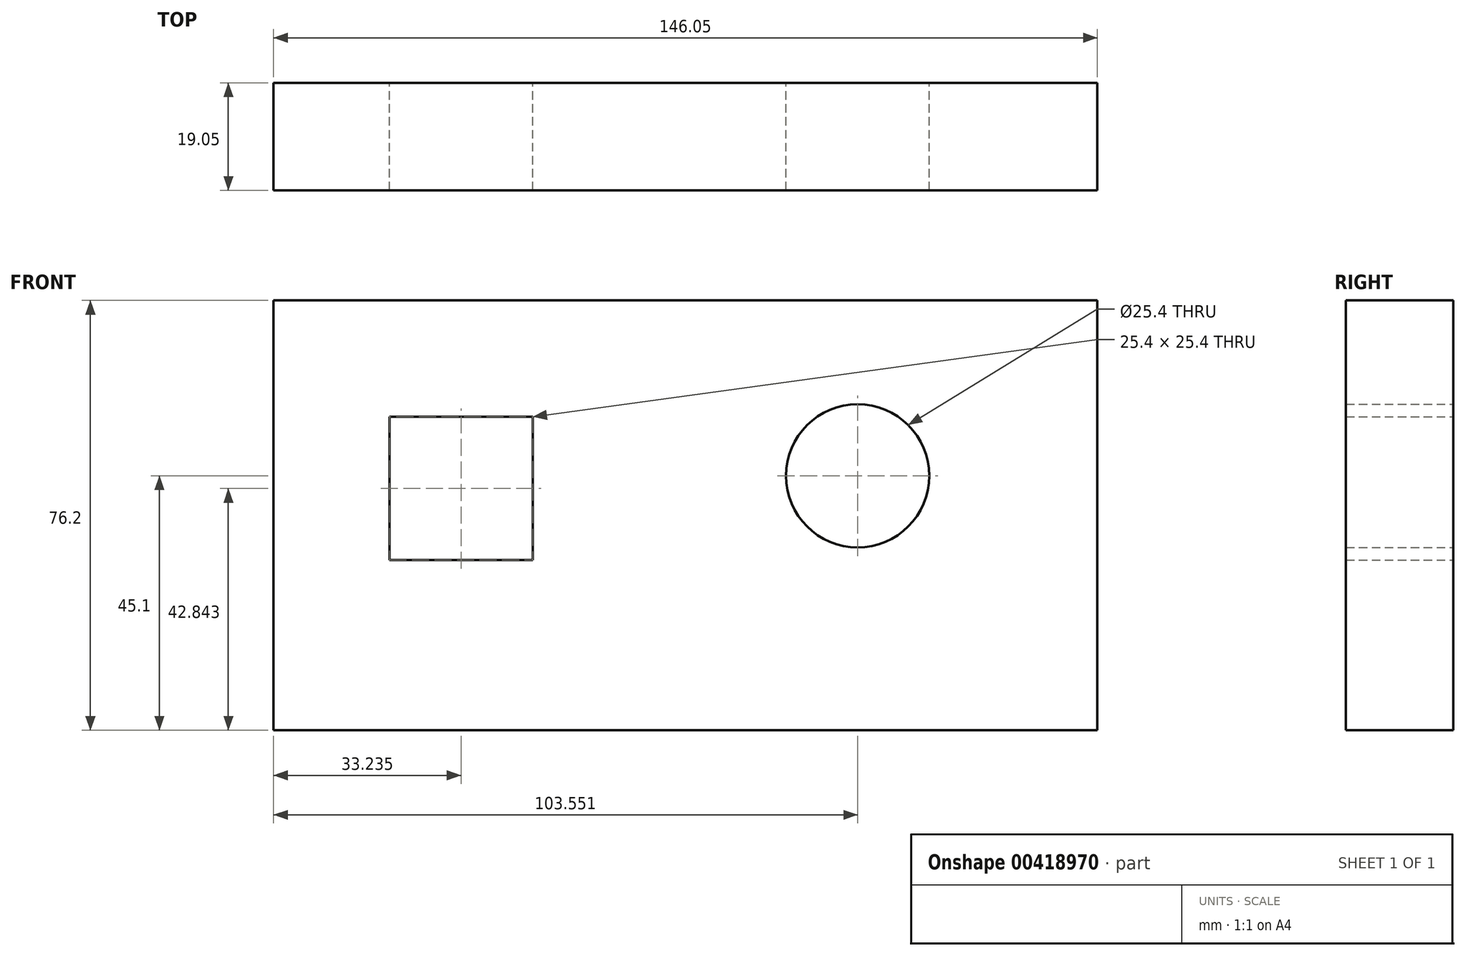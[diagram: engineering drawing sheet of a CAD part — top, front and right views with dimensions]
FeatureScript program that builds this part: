
annotation { "Feature Type Name" : "Feature", "Feature Type Description" : "" }
export const myFeature = defineFeature(function(context is Context, id is Id, definition is map)
    precondition{}
    {
        {
            var Q0;
            Q0=qCreatedBy(makeId("Front.planeOp"),FACE);
            var sketch = newSketch(context, id + "F0", { "sketchPlane" : qUnion([Q0])});
            skLineSegment(sketch, "E0.bottom", {"start": v(-73.5, 31.1) * mm, "end": v(72.55, 31.1) * mm});
            skLineSegment(sketch, "E0.top", {"start": v(-73.5, -45.1) * mm, "end": v(72.55, -45.1) * mm});
            skLineSegment(sketch, "E0.left", {"start": v(-73.5, 31.1) * mm, "end": v(-73.5, -45.1) * mm});
            skLineSegment(sketch, "E0.right", {"start": v(72.55, 31.1) * mm, "end": v(72.55, -45.1) * mm});
            skLineSegment(sketch, "E1.bottom", {"start": v(-52.97, 10.44) * mm, "end": v(-27.57, 10.44) * mm});
            skLineSegment(sketch, "E1.top", {"start": v(-52.97, -14.96) * mm, "end": v(-27.57, -14.96) * mm});
            skLineSegment(sketch, "E1.left", {"start": v(-52.97, 10.44) * mm, "end": v(-52.97, -14.96) * mm});
            skLineSegment(sketch, "E1.right", {"start": v(-27.57, 10.44) * mm, "end": v(-27.57, -14.96) * mm});
            skCircle(sketch, "E2", {"center": v(30.05, 0) * mm, "radius": 12.7 * mm});
            skSolve(sketch);
        }
        {
            var Q0;
            Q0 = qSketchRegion(id + "F0", true);
            extrude(context, id + "F1", {"entities" : qUnion([Q0]), "depth" : 19.05 * mm});
        }
    });
